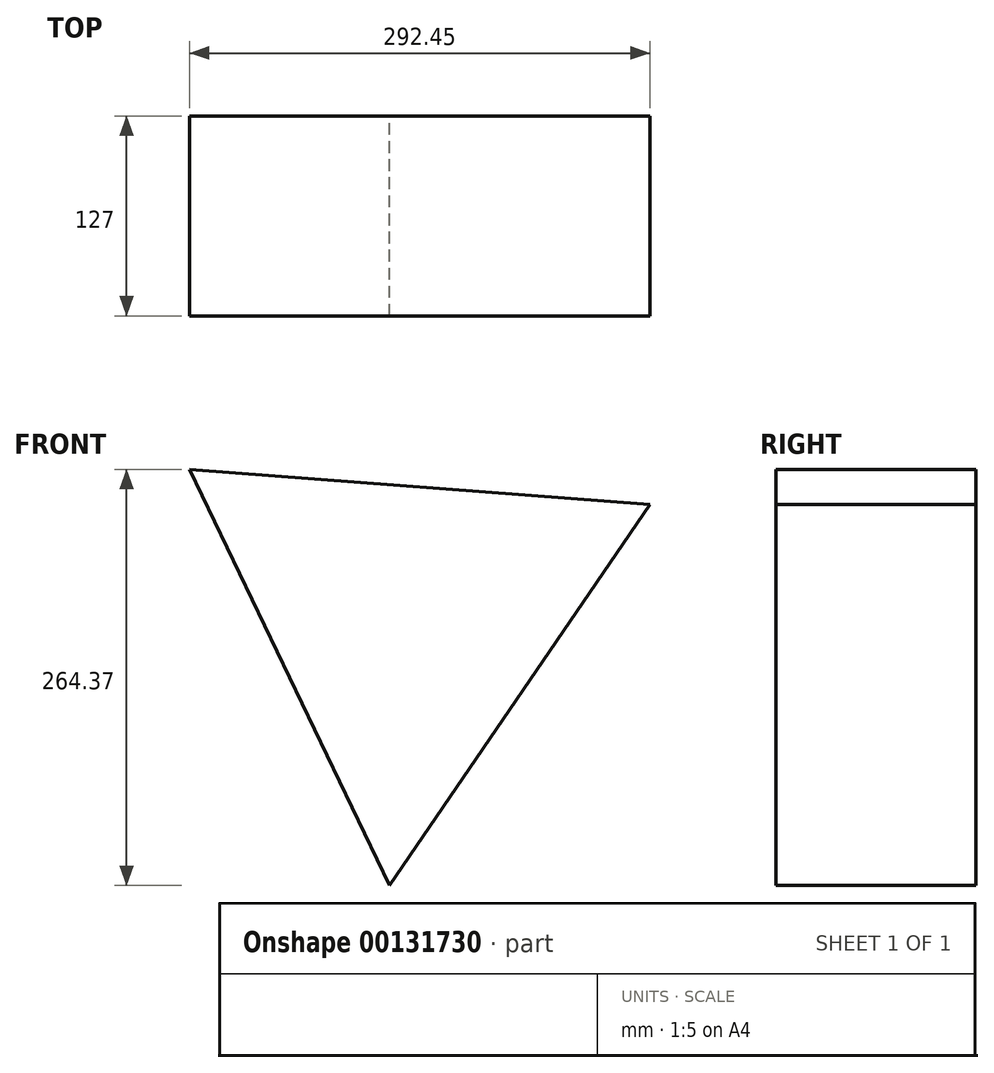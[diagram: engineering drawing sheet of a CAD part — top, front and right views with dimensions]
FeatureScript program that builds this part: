
annotation { "Feature Type Name" : "Feature", "Feature Type Description" : "" }
export const myFeature = defineFeature(function(context is Context, id is Id, definition is map)
    precondition{}
    {
        {
            var Q0;
            Q0=qCreatedBy(makeId("Front.planeOp"),FACE);
            var sketch = newSketch(context, id + "F0", { "sketchPlane" : qUnion([Q0])});
            skCircle(sketch, "E0.cCircle", {"center": v(7.46, 0) * mm, "radius": 84.67 * mm, "construction": true});
            skLineSegment(sketch, "E0.0", {"start": v(160.1, 73.32) * mm, "end": v(-5.35, -168.85) * mm});
            skLineSegment(sketch, "E0.1", {"start": v(-5.35, -168.85) * mm, "end": v(-132.35, 95.52) * mm});
            skLineSegment(sketch, "E0.2", {"start": v(-132.35, 95.52) * mm, "end": v(160.1, 73.32) * mm});
            skPoint(sketch, "E0.0.midPoint", {"position": v(77.37, -47.76) * mm});
            skSolve(sketch);
        }
        {
            var Q0;
            Q0=makeQuery(id+"F0.imprint","IMPRINT",FACE,{"disambiguationData":[TD([[makeQuery(id+"F0.imprint","IMPRINT",EDGE,{"derivedFrom":sQuery(id+"F0.wireOp",EDGE,"E0.0")}),-1.0]])]});
            extrude(context, id + "F1", {"entities" : qUnion([Q0]), "endBound" : BoundingType.SYMMETRIC, "depth" : 127 * mm});
        }
    });
